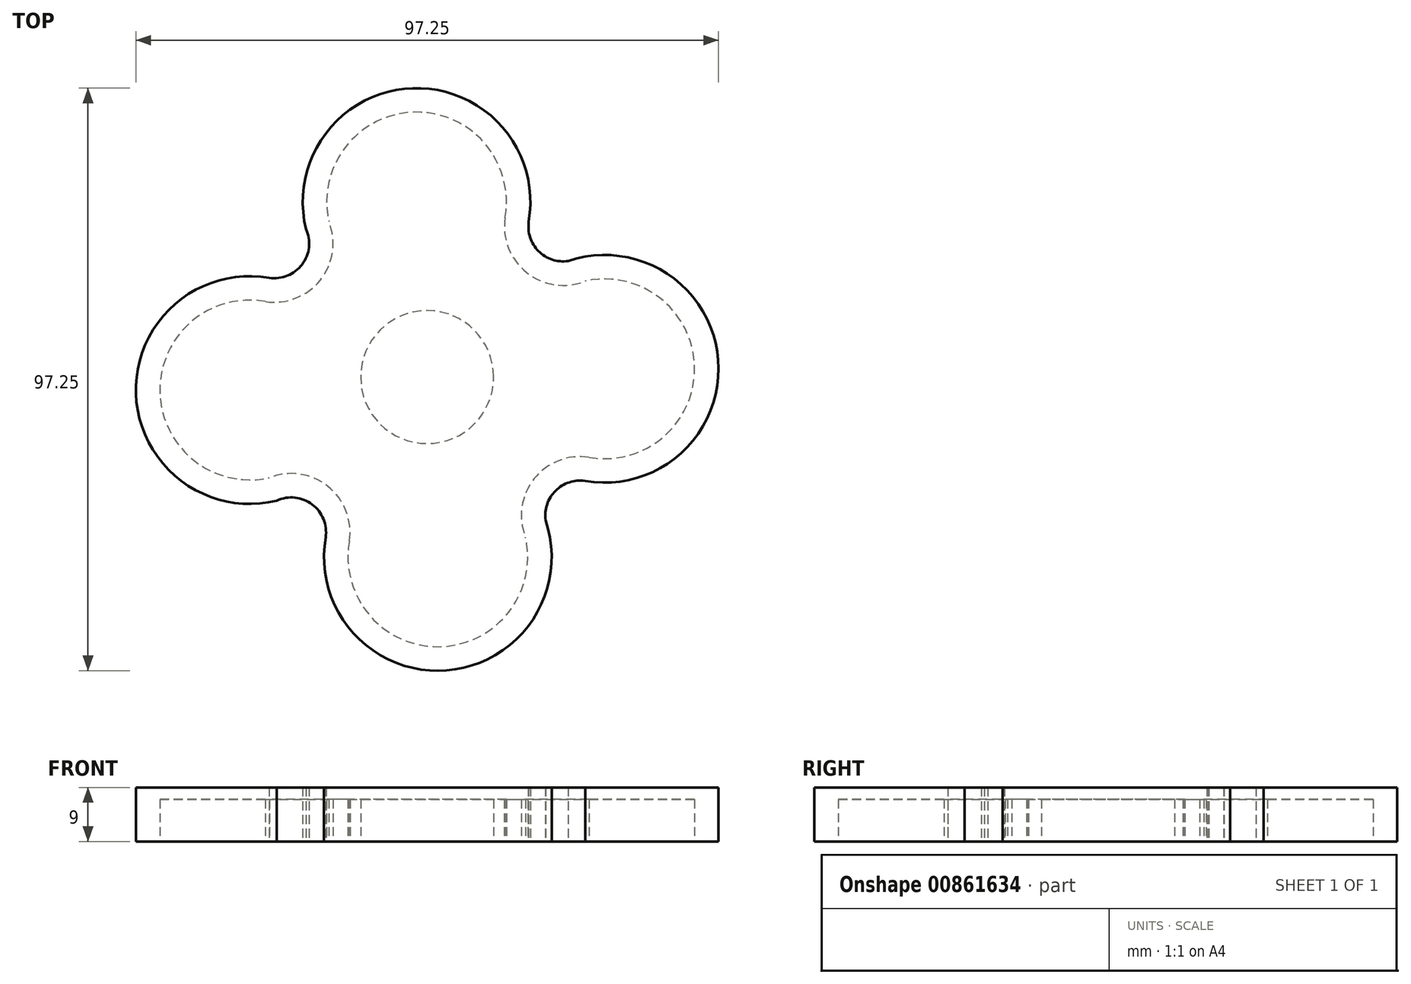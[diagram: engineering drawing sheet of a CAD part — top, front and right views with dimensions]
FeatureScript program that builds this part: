
annotation { "Feature Type Name" : "Feature", "Feature Type Description" : "" }
export const myFeature = defineFeature(function(context is Context, id is Id, definition is map)
    precondition{}
    {
        {
            var Q0;
            Q0=qCreatedBy(makeId("Top.planeOp"),FACE);
            var sketch = newSketch(context, id + "F0", { "sketchPlane" : qUnion([Q0])});
            skCircle(sketch, "E0", {"center": v(0, 0) * mm, "radius": 11.1 * mm});
            skArc(sketch, "E1", {"start": v(-13, -27.4) * mm, "mid": v(2.11, -45.02) * mm, "end": v(16.41, -26.75) * mm});
            skArc(sketch, "E2.1.0", {"start": v(27.02, -13.4) * mm, "mid": v(44.63, 1.71) * mm, "end": v(26.36, 16.01) * mm});
            skArc(sketch, "E2.2.0", {"start": v(13, 26.61) * mm, "mid": v(-2.1, 44.22) * mm, "end": v(-16.4, 25.95) * mm});
            skArc(sketch, "E2.3.0", {"start": v(-27, 12.6) * mm, "mid": v(-44.61, -2.5) * mm, "end": v(-26.34, -16.8) * mm});
            skPoint(sketch, "E2.center", {"position": v(0, -0.4) * mm});
            skArc(sketch, "E3", {"start": v(-13, -27.4) * mm, "mid": v(-16.6, -18.23) * mm, "end": v(-26.34, -16.8) * mm});
            skArc(sketch, "E4.1.0", {"start": v(27.02, -13.4) * mm, "mid": v(17.84, -17) * mm, "end": v(16.41, -26.75) * mm});
            skArc(sketch, "E4.2.0", {"start": v(13, 26.61) * mm, "mid": v(16.6, 17.44) * mm, "end": v(26.36, 16.01) * mm});
            skArc(sketch, "E4.3.0", {"start": v(-27, 12.6) * mm, "mid": v(-17.83, 16.2) * mm, "end": v(-16.4, 25.95) * mm});
            skArc(sketch, "E5.0", {"start": v(-26.36, 16.55) * mm, "mid": v(-48.6, -2.81) * mm, "end": v(-25.1, -20.62) * mm});
            skArc(sketch, "E5.1", {"start": v(-16.94, -26.76) * mm, "mid": v(-19.2, -21.27) * mm, "end": v(-25.1, -20.62) * mm});
            skArc(sketch, "E5.2", {"start": v(-26.36, 16.55) * mm, "mid": v(-20.87, 18.8) * mm, "end": v(-20.22, 24.7) * mm});
            skArc(sketch, "E5.3", {"start": v(-16.94, -26.76) * mm, "mid": v(3.24, -48.96) * mm, "end": v(19.77, -23.92) * mm});
            skArc(sketch, "E5.4", {"start": v(16.96, 25.97) * mm, "mid": v(-2.4, 48.22) * mm, "end": v(-20.22, 24.7) * mm});
            skArc(sketch, "E5.5", {"start": v(16.96, 25.97) * mm, "mid": v(18.59, 21.02) * mm, "end": v(23.53, 19.37) * mm});
            skArc(sketch, "E5.6", {"start": v(26.37, -17.35) * mm, "mid": v(48.57, 2.84) * mm, "end": v(23.53, 19.37) * mm});
            skArc(sketch, "E5.7", {"start": v(26.37, -17.35) * mm, "mid": v(21.43, -18.98) * mm, "end": v(19.77, -23.92) * mm});
            skSolve(sketch);
        }
        {
            var Q0;
            Q0=makeQuery(id+"F0.imprint","IMPRINT",FACE,{"disambiguationData":[TD([[makeQuery(id+"F0.imprint","IMPRINT",EDGE,{"derivedFrom":sQuery(id+"F0.wireOp",EDGE,"E0")}),-1.0]])]});
            extrude(context, id + "F1", {"entities" : qUnion([Q0]), "depth" : 7 * mm, "offsetDistance" : 25 * mm});
        }
        {
            var Q0;
            Q0 = qSketchRegion(id + "F0", true);
            var Q1;
            Q1=makeQuery(id+"F0.imprint","IMPRINT",FACE,{"disambiguationData":[TD([[makeQuery(id+"F0.imprint","IMPRINT",EDGE,{"derivedFrom":sQuery(id+"F0.wireOp",EDGE,"E0")}),-1.0]])]});
            var Q2;
            Q2=makeQuery(id+"F0.imprint","IMPRINT",FACE,{"disambiguationData":[TD([[makeQuery(id+"F0.imprint","IMPRINT",EDGE,{"derivedFrom":sQuery(id+"F0.wireOp",EDGE,"E0")}),1.0]])]});
            extrude(context, id + "F2", {"entities" : qUnion([Q0, Q1, Q2]), "depth" : 9 * mm, "offsetDistance" : 25 * mm});
        }
        {
            var Q0;
            Q0=makeQuery(id+"F1.opExtrude","SWEPT_BODY",BODY,{"disambiguationData":[OSD([sQuery(id+"F0.wireOp",EDGE,"E0"),sQuery(id+"F0.wireOp",EDGE,"E1"),sQuery(id+"F0.wireOp",EDGE,"E2.1.0"),sQuery(id+"F0.wireOp",EDGE,"E2.2.0"),sQuery(id+"F0.wireOp",EDGE,"E2.3.0"),sQuery(id+"F0.wireOp",EDGE,"E3"),sQuery(id+"F0.wireOp",EDGE,"E4.1.0"),sQuery(id+"F0.wireOp",EDGE,"E4.2.0"),sQuery(id+"F0.wireOp",EDGE,"E4.3.0")])]});
            var Q1;
            Q1=makeQuery(id+"F2.opExtrude","SWEPT_BODY",BODY,{"disambiguationData":[OSD([sQuery(id+"F0.wireOp",EDGE,"E5.0"),sQuery(id+"F0.wireOp",EDGE,"E5.1"),sQuery(id+"F0.wireOp",EDGE,"E5.2"),sQuery(id+"F0.wireOp",EDGE,"E5.3"),sQuery(id+"F0.wireOp",EDGE,"E5.4"),sQuery(id+"F0.wireOp",EDGE,"E5.5"),sQuery(id+"F0.wireOp",EDGE,"E5.6"),sQuery(id+"F0.wireOp",EDGE,"E5.7")])]});
            booleanBodies(context, id + "F3", {"operationType" : BooleanOperationType.SUBTRACTION, "tools" : qUnion([Q0]), "targets" : qUnion([Q1])});
        }
    });
